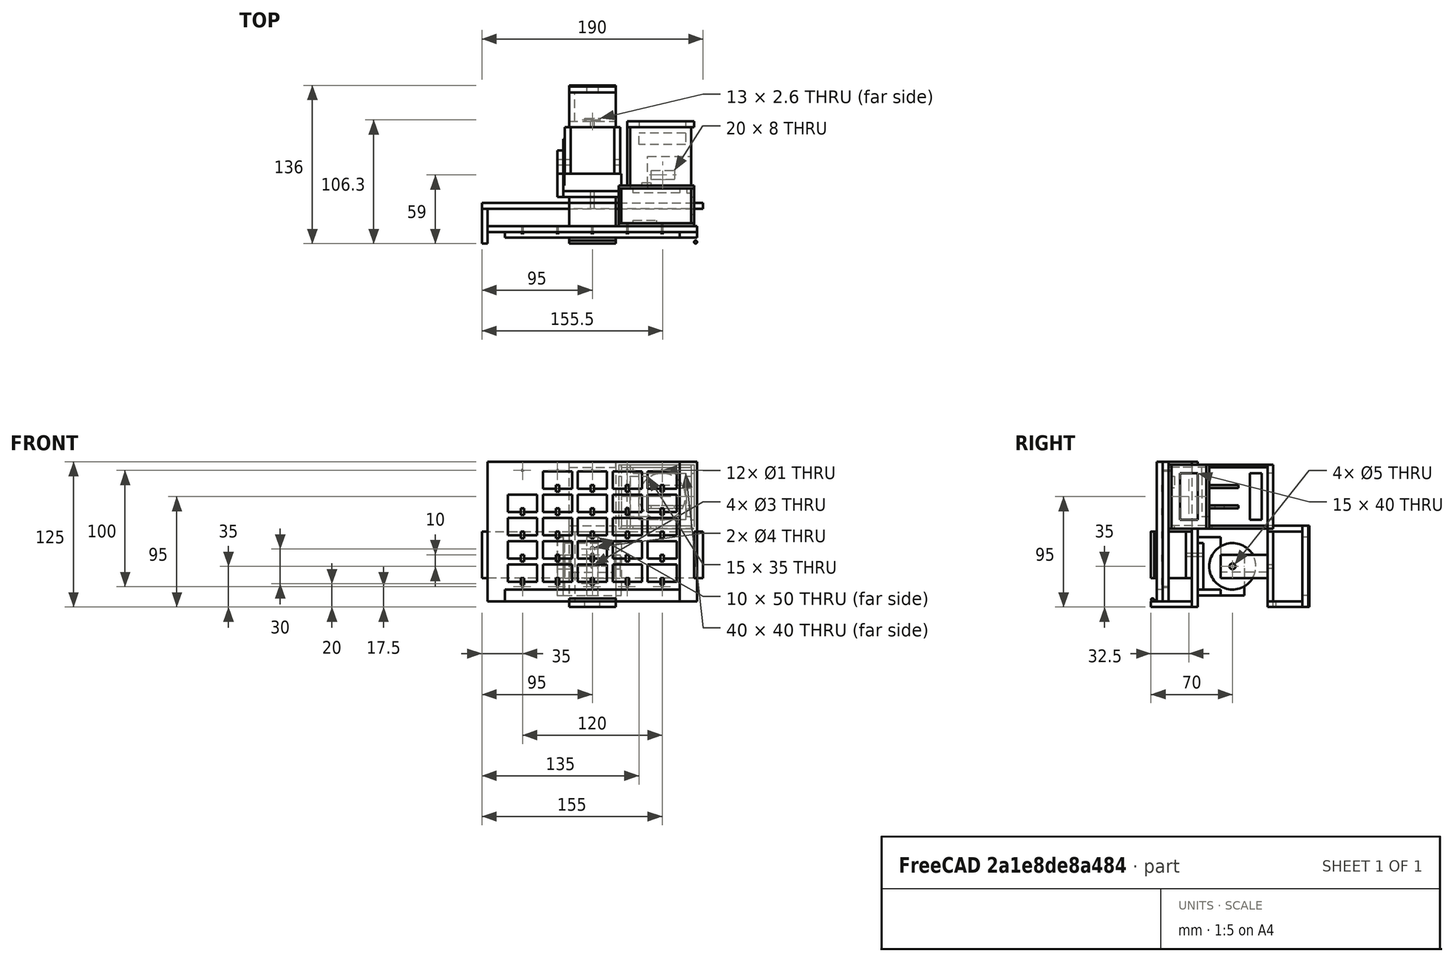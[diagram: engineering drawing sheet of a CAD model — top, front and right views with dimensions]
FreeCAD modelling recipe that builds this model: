
FCSTD DOCUMENT  (FreeCAD 0.15R4671 (Git))
Label: light
License: All rights reserved
LicenseURL: http://en.wikipedia.org/wiki/All_rights_reserved
objects: Sketcher::SketchObject×40, PartDesign::Pad×40, Part::FeaturePython×21, App::DocumentObjectGroup×10, Mesh::Feature×1
note: 141 computed .brp shape members not serialized (recipe doc carries the construction recipe); baked Part::Feature solids carry a one-line shape summary decoded from their .brp

FEATURE [Sketcher::SketchObject] Sketch
  Placement = pos=(0,0,0) rot=(1,0,0;1.5708rad)
  sketch-geometry (14):
    g0: LineSegment StartX=-90 StartY=60 StartZ=0 EndX=90 EndY=60 EndZ=0
    g1: LineSegment StartX=90 StartY=60 StartZ=0 EndX=90 EndY=-60 EndZ=0
    g2: LineSegment StartX=90 StartY=-60 StartZ=0 EndX=-90 EndY=-60 EndZ=0
    g3: LineSegment StartX=-90 StartY=-60 StartZ=0 EndX=-90 EndY=60 EndZ=0
    g4: Circle CenterX=-60 CenterY=52.5 CenterZ=0 NormalX=0 NormalY=0 NormalZ=1 Radius=0.5
    g5: Circle CenterX=-30 CenterY=52.5 CenterZ=0 NormalX=0 NormalY=0 NormalZ=1 Radius=0.5
    g6: Circle CenterX=0 CenterY=52.5 CenterZ=0 NormalX=0 NormalY=0 NormalZ=1 Radius=0.5
    g7: Circle CenterX=30 CenterY=52.5 CenterZ=0 NormalX=0 NormalY=0 NormalZ=1 Radius=0.5
    g8: Circle CenterX=60 CenterY=52.5 CenterZ=0 NormalX=0 NormalY=0 NormalZ=1 Radius=0.5
    g9: Circle CenterX=-60 CenterY=-47.5 CenterZ=0 NormalX=0 NormalY=0 NormalZ=1 Radius=0.5
    g10: Circle CenterX=-30 CenterY=-47.5 CenterZ=0 NormalX=0 NormalY=0 NormalZ=1 Radius=0.5
    g11: Circle CenterX=0 CenterY=-47.5 CenterZ=0 NormalX=0 NormalY=0 NormalZ=1 Radius=0.5
    g12: Circle CenterX=30 CenterY=-47.5 CenterZ=0 NormalX=0 NormalY=0 NormalZ=1 Radius=0.5
    g13: Circle CenterX=60 CenterY=-47.5 CenterZ=0 NormalX=0 NormalY=0 NormalZ=1 Radius=0.5
  constraints (36):
    c: Coincident(g0,g1)
    c: Coincident(g1,g2)
    c: Coincident(g2,g3)
    c: Coincident(g3,g0)
    c: Horizontal(g0)
    c: Horizontal(g2)
    c: Vertical(g1)
    c: Vertical(g3)
    c: Symmetric(g0,g0,g-2)
    c: DistanceX(g0,g0) = 180
    c: DistanceY(g3,g3) = 120
    c: Symmetric(g0,g2,g-1)
    c: Radius(g4) = 0.5
    c: Radius(g5) = 0.5
    c: DistanceY(g4,g0) = 7.5
    c: DistanceY(g5,g0) = 7.5
    c: DistanceX(g4,g5) = 30
    c: Equal(g5,g6) = 0.5
    c: DistanceY(g6,g0) = 7.5
    c: DistanceX(g5,g6) = 30
    c: DistanceY(g7,g0) = 7.5
    c: DistanceX(g6,g7) = 30
    c: DistanceY(g8,g0) = 7.5
    c: DistanceX(g7,g8) = 30
    c: Radius(g9) = 0.5
    c: DistanceY(g2,g9) = 12.5
    c: DistanceX(g2,g9) = 30
    c: Equal(g9,g10) = 0.5
    c: DistanceY(g2,g10) = 12.5
    c: DistanceX(g9,g10) = 30
    c: DistanceY(g2,g11) = 12.5
    c: DistanceX(g10,g11) = 30
    c: DistanceY(g1,g12) = 12.5
    c: DistanceX(g11,g12) = 30
    c: DistanceY(g1,g13) = 12.5
    c: DistanceX(g12,g13) = 30
FEATURE [PartDesign::Pad] Pad
  Length = 5
  Length2 = 100
  Placement = pos=(0,0,0) rot=(1,0,0;1.5708rad)
  Sketch = -> Sketch
  Type = 0
FEATURE [Sketcher::SketchObject] Sketch003
  Placement = pos=(0,-5,0) rot=(1,0,0;1.5708rad)
  sketch-geometry (4):
    g0: LineSegment StartX=-61.5 StartY=40 StartZ=0 EndX=-58.5 EndY=40 EndZ=0
    g1: LineSegment StartX=-58.5 StartY=40 StartZ=0 EndX=-58.5 EndY=34.3 EndZ=0
    g2: LineSegment StartX=-58.5 StartY=34.3 StartZ=0 EndX=-61.5 EndY=34.3 EndZ=0
    g3: LineSegment StartX=-61.5 StartY=34.3 StartZ=0 EndX=-61.5 EndY=40 EndZ=0
  constraints (12):
    c: Coincident(g0,g1)
    c: Coincident(g1,g2)
    c: Coincident(g2,g3)
    c: Coincident(g3,g0)
    c: Horizontal(g0)
    c: Horizontal(g2)
    c: Vertical(g1)
    c: Vertical(g3)
    c: DistanceX(g0,g0) = 3
    c: DistanceY(g3,g3) = 5.7
    c: DistanceY(g-1,g0) = 40
    c: DistanceX(g1,g-1) = 58.5
FEATURE [PartDesign::Pad] Pad003
  Length = 0.9
  Length2 = 100
  Placement = pos=(0,-5,0) rot=(1,0,0;1.5708rad)
  Sketch = -> Sketch003
  Type = 0
FEATURE [Part::FeaturePython] Clone  label="Clone of Pad003"  # Draft clone (typed FeaturePython)
  Objects = -> [Pad003]
  Placement = pos=(0,-5,-20) rot=(1,0,0;1.5708rad)
  Scale = (1,1,1)
FEATURE [Part::FeaturePython] Clone001  label="Clone of Pad004"  # Draft clone (typed FeaturePython)
  Objects = -> [Pad003]
  Placement = pos=(0,-5,-40) rot=(1,0,0;1.5708rad)
  Scale = (1,1,1)
FEATURE [Part::FeaturePython] Clone002  label="Clone of Pad005"  # Draft clone (typed FeaturePython)
  Objects = -> [Pad003]
  Placement = pos=(0,-5,-60) rot=(1,0,0;1.5708rad)
  Scale = (1,1,1)
FEATURE [Part::FeaturePython] Clone003  label="Clone of Pad006"  # Draft clone (typed FeaturePython)
  Objects = -> [Pad003]
  Placement = pos=(0,-5,-80) rot=(1,0,0;1.5708rad)
  Scale = (1,1,1)
FEATURE [Sketcher::SketchObject] Sketch004
  Placement = pos=(90,0,0) rot=(0.57735,0.57735,0.57735;2.0944rad)
  sketch-geometry (4):
    g0: LineSegment StartX=-15 StartY=0 StartZ=0 EndX=15 EndY=0 EndZ=0
    g1: LineSegment StartX=15 StartY=0 StartZ=0 EndX=15 EndY=-40 EndZ=0
    g2: LineSegment StartX=15 StartY=-40 StartZ=0 EndX=-15 EndY=-40 EndZ=0
    g3: LineSegment StartX=-15 StartY=-40 StartZ=0 EndX=-15 EndY=0 EndZ=0
  constraints (12):
    c: Coincident(g0,g1)
    c: Coincident(g1,g2)
    c: Coincident(g2,g3)
    c: Coincident(g3,g0)
    c: Horizontal(g0)
    c: Horizontal(g2)
    c: Vertical(g1)
    c: Vertical(g3)
    c: DistanceX(g0,g0) = 30
    c: DistanceY(g1,g1) = 40
    c: DistanceX(g-1,g0) = 15
    c: PointOnObject(g0,g-1)
FEATURE [PartDesign::Pad] Pad004
  Length = 5
  Length2 = 100
  Placement = pos=(90,0,0) rot=(0.57735,0.57735,0.57735;2.0944rad)
  Sketch = -> Sketch004
  Type = 0
FEATURE [Part::FeaturePython] Clone008  label="Clone of Pad007"  # Draft clone (typed FeaturePython)
  Objects = -> [Pad004]
  Placement = pos=(-95,0,0) rot=(0.57735,0.57735,0.57735;2.0944rad)
  Scale = (1,1,1)
FEATURE [Sketcher::SketchObject] Sketch005
  Placement = pos=(0,20,0) rot=(1,0,0;1.5708rad)
  sketch-geometry (5):
    g0: LineSegment StartX=-95 StartY=0 StartZ=0 EndX=95 EndY=0 EndZ=0
    g1: LineSegment StartX=95 StartY=0 StartZ=0 EndX=95 EndY=-40 EndZ=0
    g2: LineSegment StartX=95 StartY=-40 StartZ=0 EndX=-95 EndY=-40 EndZ=0
    g3: LineSegment StartX=-95 StartY=-40 StartZ=0 EndX=-95 EndY=0 EndZ=0
    g4: Circle CenterX=0 CenterY=-20 CenterZ=0 NormalX=0 NormalY=0 NormalZ=1 Radius=1.5
  constraints (15):
    c: Coincident(g0,g1)
    c: Coincident(g1,g2)
    c: Coincident(g2,g3)
    c: Coincident(g3,g0)
    c: Horizontal(g0)
    c: Horizontal(g2)
    c: Vertical(g1)
    c: Vertical(g3)
    c: DistanceX(g0,g0) = 190
    c: DistanceY(g3,g3) = 40
    c: Symmetric(g1,g2,g-2)
    c: PointOnObject(g0,g-1)
    c: PointOnObject(g4,g-2)
    c: Radius(g4) = 1.5
    c: DistanceY(g4,g0) = 20
FEATURE [PartDesign::Pad] Pad005
  Length = 5
  Length2 = 100
  Placement = pos=(0,20,0) rot=(1,0,0;1.5708rad)
  Sketch = -> Sketch005
  Type = 0
FEATURE [Sketcher::SketchObject] Sketch006
  Placement = pos=(0,0,55) rot=(0,0,1;0rad)
  sketch-geometry (4):
    g0: LineSegment StartX=-20 StartY=20 StartZ=0 EndX=20 EndY=20 EndZ=0
    g1: LineSegment StartX=20 StartY=20 StartZ=0 EndX=20 EndY=0 EndZ=0
    g2: LineSegment StartX=20 StartY=0 StartZ=0 EndX=-20 EndY=0 EndZ=0
    g3: LineSegment StartX=-20 StartY=0 StartZ=0 EndX=-20 EndY=20 EndZ=0
  constraints (12):
    c: Coincident(g0,g1)
    c: Coincident(g1,g2)
    c: Coincident(g2,g3)
    c: Coincident(g3,g0)
    c: Horizontal(g0)
    c: Horizontal(g2)
    c: Vertical(g1)
    c: Vertical(g3)
    c: PointOnObject(g1,g-1)
    c: Symmetric(g0,g0,g-2)
    c: DistanceX(g0,g0) = 40
    c: DistanceY(g3,g3) = 20
FEATURE [PartDesign::Pad] Pad006
  Length = 5
  Length2 = 100
  Placement = pos=(0,0,55) rot=(0,0,1;0rad)
  Sketch = -> Sketch006
  Type = 0
FEATURE [Sketcher::SketchObject] Sketch007
  Placement = pos=(0,25,0) rot=(1,0,0;1.5708rad)
  sketch-geometry (5):
    g0: LineSegment StartX=-20 StartY=60 StartZ=0 EndX=20 EndY=60 EndZ=0
    g1: LineSegment StartX=20 StartY=60 StartZ=0 EndX=20 EndY=-65 EndZ=0
    g2: LineSegment StartX=20 StartY=-65 StartZ=0 EndX=-20 EndY=-65 EndZ=0
    g3: LineSegment StartX=-20 StartY=-65 StartZ=0 EndX=-20 EndY=60 EndZ=0
    g4: Circle CenterX=0 CenterY=-20 CenterZ=0 NormalX=0 NormalY=0 NormalZ=1 Radius=1.5
  constraints (15):
    c: Coincident(g0,g1)
    c: Coincident(g1,g2)
    c: Coincident(g2,g3)
    c: Coincident(g3,g0)
    c: Horizontal(g0)
    c: Horizontal(g2)
    c: Vertical(g1)
    c: Vertical(g3)
    c: DistanceY(g3,g3) = 125
    c: Symmetric(g0,g0,g-2)
    c: DistanceX(g0,g0) = 40
    c: DistanceY(g1,g-1) = 65
    c: PointOnObject(g4,g-2)
    c: Radius(g4) = 1.5
    c: DistanceY(g4,g-1) = 20
FEATURE [PartDesign::Pad] Pad007
  Length = 5
  Length2 = 100
  Placement = pos=(0,25,0) rot=(1,0,0;1.5708rad)
  Sketch = -> Sketch007
  Type = 0
FEATURE [Sketcher::SketchObject] Sketch008
  Placement = pos=(25,0,0) rot=(0.57735,0.57735,0.57735;2.0944rad)
  sketch-geometry (7):
    g0: LineSegment StartX=65 StartY=-20 StartZ=0 EndX=65 EndY=-55 EndZ=0
    g1: LineSegment StartX=65 StartY=-55 StartZ=0 EndX=25 EndY=-55 EndZ=0
    g2: LineSegment StartX=25 StartY=-55 StartZ=0 EndX=25 EndY=-5 EndZ=0
    g3: Circle CenterX=55 CenterY=-30 CenterZ=0 NormalX=0 NormalY=0 NormalZ=1 Radius=2.5
    g4: LineSegment StartX=25 StartY=-5 StartZ=0 EndX=45 EndY=-5 EndZ=0
    g5: LineSegment StartX=45 StartY=-5 StartZ=0 EndX=45 EndY=-20 EndZ=0
    g6: LineSegment StartX=45 StartY=-20 StartZ=0 EndX=65 EndY=-20 EndZ=0
  constraints (21):
    c: Coincident(g0,g1)
    c: Coincident(g1,g2)
    c: Horizontal(g1)
    c: Vertical(g0)
    c: Vertical(g2)
    c: DistanceX(g2,g0) = 40
    c: DistanceY(g0,g0) = 35
    c: DistanceX(g1) = 25
    c: Radius(g3) = 2.5
    c: DistanceX(g3,g0) = 10
    c: DistanceY(g3,g0) = 10
    c: DistanceY(g0,g-1) = 20
    c: Horizontal(g4)
    c: Coincident(g4,g5)
    c: Vertical(g5)
    c: Coincident(g5,g6)
    c: Horizontal(g6)
    c: DistanceY(g5) = -15
    c: Coincident(g2,g4)
    c: Coincident(g0,g6)
    c: DistanceX(g4) = 20
FEATURE [PartDesign::Pad] Pad008
  Length = 5
  Length2 = 100
  Placement = pos=(25,0,0) rot=(0.57735,0.57735,0.57735;2.0944rad)
  Sketch = -> Sketch008
  Type = 0
FEATURE [Sketcher::SketchObject] Sketch010
  Placement = pos=(0,0,-10) rot=(0,0,1;0rad)
  sketch-geometry (4):
    g0: LineSegment StartX=-25 StartY=45 StartZ=0 EndX=25 EndY=45 EndZ=0
    g1: LineSegment StartX=25 StartY=45 StartZ=0 EndX=25 EndY=25 EndZ=0
    g2: LineSegment StartX=25 StartY=25 StartZ=0 EndX=-25 EndY=25 EndZ=0
    g3: LineSegment StartX=-25 StartY=25 StartZ=0 EndX=-25 EndY=45 EndZ=0
  constraints (12):
    c: Coincident(g0,g1)
    c: Coincident(g1,g2)
    c: Coincident(g2,g3)
    c: Coincident(g3,g0)
    c: Horizontal(g0)
    c: Horizontal(g2)
    c: Vertical(g1)
    c: Vertical(g3)
    c: DistanceX(g0,g0) = 50
    c: DistanceY(g3,g3) = 20
    c: Symmetric(g1,g2,g-2)
    c: DistanceY(g-1,g2) = 25
FEATURE [PartDesign::Pad] Pad010
  Length = 5
  Length2 = 100
  Placement = pos=(0,0,-10) rot=(0,0,1;0rad)
  Sketch = -> Sketch010
  Type = 0
FEATURE [Part::FeaturePython] Clone010  label="Clone of Pad010"  # Draft clone (typed FeaturePython)
  Objects = -> [Pad010]
  Placement = pos=(0,0,-55) rot=(0,0,1;0rad)
  Scale = (1,1,1)
FEATURE [Sketcher::SketchObject] Sketch011
  Placement = pos=(18.75,0,0) rot=(0.57735,0.57735,0.57735;2.0944rad)
  sketch-geometry (5):
    g0: LineSegment StartX=45 StartY=-20 StartZ=0 EndX=85 EndY=-20 EndZ=0
    g1: LineSegment StartX=85 StartY=-20 StartZ=0 EndX=85 EndY=-40 EndZ=0
    g2: LineSegment StartX=85 StartY=-40 StartZ=0 EndX=45 EndY=-40 EndZ=0
    g3: LineSegment StartX=45 StartY=-40 StartZ=0 EndX=45 EndY=-20 EndZ=0
    g4: Circle CenterX=55 CenterY=-30 CenterZ=0 NormalX=0 NormalY=0 NormalZ=1 Radius=2.5
  constraints (15):
    c: Coincident(g0,g1)
    c: Coincident(g1,g2)
    c: Coincident(g2,g3)
    c: Coincident(g3,g0)
    c: Horizontal(g0)
    c: Horizontal(g2)
    c: Vertical(g1)
    c: Vertical(g3)
    c: DistanceY(g1,g1) = 20
    c: DistanceX(g0,g0) = 40
    c: DistanceX(g-1,g0) = 45
    c: Radius(g4) = 2.5
    c: DistanceX(g0,g4) = 10
    c: DistanceY(g0,g-1) = 20
    c: DistanceY(g4,g0) = 10
FEATURE [PartDesign::Pad] Pad011
  Length = 5
  Length2 = 100
  Placement = pos=(18.75,0,0) rot=(0.57735,0.57735,0.57735;2.0944rad)
  Sketch = -> Sketch011
  Type = 0
FEATURE [Sketcher::SketchObject] Sketch012
  Placement = pos=(0,0,-25) rot=(0,0,1;0rad)
  sketch-geometry (4):
    g0: LineSegment StartX=-18.75 StartY=85 StartZ=0 EndX=18.75 EndY=85 EndZ=0
    g1: LineSegment StartX=18.75 StartY=85 StartZ=0 EndX=18.75 EndY=45 EndZ=0
    g2: LineSegment StartX=18.75 StartY=45 StartZ=0 EndX=-18.75 EndY=45 EndZ=0
    g3: LineSegment StartX=-18.75 StartY=45 StartZ=0 EndX=-18.75 EndY=85 EndZ=0
  constraints (12):
    c: Coincident(g0,g1)
    c: Coincident(g1,g2)
    c: Coincident(g2,g3)
    c: Coincident(g3,g0)
    c: Horizontal(g0)
    c: Horizontal(g2)
    c: Vertical(g1)
    c: Vertical(g3)
    c: DistanceX(g0,g0) = 37.5
    c: DistanceY(g3,g3) = 40
    c: Symmetric(g0,g0,g-2)
    c: DistanceY(g-1,g1) = 45
FEATURE [PartDesign::Pad] Pad012
  Length = 5
  Length2 = 100
  Placement = pos=(0,0,-25) rot=(0,0,1;0rad)
  Sketch = -> Sketch012
  Type = 0
FEATURE [Part::FeaturePython] Clone012  label="Clone of Pad012"  # Draft clone (typed FeaturePython)
  Objects = -> [Pad012]
  Placement = pos=(0,0,-40) rot=(0,0,1;0rad)
  Scale = (1,1,1)
FEATURE [Part::FeaturePython] Clone013  label="Clone of Pad013"  # Draft clone (typed FeaturePython)
  Objects = -> [Pad008]
  Placement = pos=(-30,0,0) rot=(0.57735,0.57735,0.57735;2.0944rad)
  Scale = (1,1,1)
FEATURE [Sketcher::SketchObject] Sketch013
  Placement = pos=(0,0,-65) rot=(0,0,1;0rad)
  sketch-geometry (4):
    g0: LineSegment StartX=-20 StartY=20 StartZ=0 EndX=20 EndY=20 EndZ=0
    g1: LineSegment StartX=20 StartY=20 StartZ=0 EndX=20 EndY=-15 EndZ=0
    g2: LineSegment StartX=20 StartY=-15 StartZ=0 EndX=-20 EndY=-15 EndZ=0
    g3: LineSegment StartX=-20 StartY=-15 StartZ=0 EndX=-20 EndY=20 EndZ=0
  constraints (12):
    c: Coincident(g0,g1)
    c: Coincident(g1,g2)
    c: Coincident(g2,g3)
    c: Coincident(g3,g0)
    c: Horizontal(g0)
    c: Horizontal(g2)
    c: Vertical(g1)
    c: Vertical(g3)
    c: Symmetric(g0,g0,g-2)
    c: DistanceX(g0,g0) = 40
    c: DistanceY(g3,g3) = 35
    c: DistanceY(g-1,g0) = 20
FEATURE [PartDesign::Pad] Pad013
  Length = 5
  Length2 = 100
  Placement = pos=(0,0,-65) rot=(0,0,1;0rad)
  Sketch = -> Sketch013
  Type = 0
FEATURE [Sketcher::SketchObject] Sketch014
  Placement = pos=(0,0,-40) rot=(0,0,1;0rad)
  sketch-geometry (1):
    g0: Circle CenterX=-88.7 CenterY=-13.7 CenterZ=0 NormalX=0 NormalY=0 NormalZ=1 Radius=1.3
  constraints (3):
    c: Radius(g0) = 1.3
    c: DistanceX(g0) = -88.7
    c: DistanceY(g0) = -13.7
FEATURE [PartDesign::Pad] Pad014
  Length = 40
  Length2 = 100
  Placement = pos=(0,0,-40) rot=(0,0,1;0rad)
  Sketch = -> Sketch014
  Type = 0
FEATURE [Part::FeaturePython] Clone014  label="Clone of Pad014"  # Draft clone (typed FeaturePython)
  Objects = -> [Pad014]
  Placement = pos=(177.4,0,-40) rot=(0,0,1;0rad)
  Scale = (1,1,1)
FEATURE [App::DocumentObjectGroup] Group002  label="HFrame"
  Group = -> [Pad005,Pad004,Clone008,Pad014,Clone014]
FEATURE [Sketcher::SketchObject] Sketch015
  Placement = pos=(-20,0,0) rot=(0.57735,0.57735,0.57735;2.0944rad)
  sketch-geometry (1):
    g0: Circle CenterX=-13.7 CenterY=-58.7 CenterZ=0 NormalX=0 NormalY=0 NormalZ=1 Radius=1.3
  constraints (3):
    c: Radius(g0) = 1.3
    c: DistanceX(g0) = -13.7
    c: DistanceY(g0) = -58.7
FEATURE [PartDesign::Pad] Pad015
  Length = 40
  Length2 = 100
  Placement = pos=(-20,0,0) rot=(0.57735,0.57735,0.57735;2.0944rad)
  Sketch = -> Sketch015
  Type = 0
FEATURE [App::DocumentObjectGroup] Group003  label="VFrame"
  Group = -> [Pad006,Pad007,Pad013,Pad015]
FEATURE [Sketcher::SketchObject] Sketch016
  Placement = pos=(0,90,0) rot=(1,0,0;1.5708rad)
  sketch-geometry (5):
    g0: LineSegment StartX=-20 StartY=0 StartZ=0 EndX=20 EndY=0 EndZ=0
    g1: LineSegment StartX=20 StartY=0 StartZ=0 EndX=20 EndY=-60 EndZ=0
    g2: LineSegment StartX=20 StartY=-60 StartZ=0 EndX=-20 EndY=-60 EndZ=0
    g3: LineSegment StartX=-20 StartY=-60 StartZ=0 EndX=-20 EndY=0 EndZ=0
    g4: Circle CenterX=0 CenterY=-30 CenterZ=0 NormalX=0 NormalY=0 NormalZ=1 Radius=1.5
  constraints (14):
    c: Coincident(g0,g1)
    c: Coincident(g1,g2)
    c: Coincident(g2,g3)
    c: Coincident(g3,g0)
    c: Horizontal(g0)
    c: Horizontal(g2)
    c: Vertical(g1)
    c: Vertical(g3)
    c: Symmetric(g0,g0,g-2)
    c: DistanceX(g0,g0) = 40
    c: DistanceY(g1,g1) = 60
    c: DistanceY(g0) = 0
    c: Radius(g4) = 1.5
    c: DistanceY(g4,g0) = 30
FEATURE [PartDesign::Pad] Pad016
  Length = 5
  Length2 = 100
  Placement = pos=(0,90,0) rot=(1,0,0;1.5708rad)
  Sketch = -> Sketch016
  Type = 0
FEATURE [Sketcher::SketchObject] Sketch017
  Placement = pos=(15,0,0) rot=(0.57735,0.57735,0.57735;2.0944rad)
  sketch-geometry (4):
    g0: LineSegment StartX=90 StartY=0 StartZ=0 EndX=115 EndY=0 EndZ=0
    g1: LineSegment StartX=115 StartY=0 StartZ=0 EndX=115 EndY=-60 EndZ=0
    g2: LineSegment StartX=115 StartY=-60 StartZ=0 EndX=90 EndY=-60 EndZ=0
    g3: LineSegment StartX=90 StartY=-60 StartZ=0 EndX=90 EndY=0 EndZ=0
  constraints (12):
    c: Coincident(g0,g1)
    c: Coincident(g1,g2)
    c: Coincident(g2,g3)
    c: Coincident(g3,g0)
    c: Horizontal(g0)
    c: Horizontal(g2)
    c: Vertical(g1)
    c: Vertical(g3)
    c: PointOnObject(g0,g-1)
    c: DistanceX(g0,g0) = 25
    c: DistanceY(g1,g1) = 60
    c: DistanceX(g-1,g0) = 90
FEATURE [PartDesign::Pad] Pad017
  Length = 5
  Length2 = 100
  Placement = pos=(15,0,0) rot=(0.57735,0.57735,0.57735;2.0944rad)
  Sketch = -> Sketch017
  Type = 0
FEATURE [Part::FeaturePython] Clone015  label="Clone of Pad017"  # Draft clone (typed FeaturePython)
  Objects = -> [Pad017]
  Placement = pos=(-20,0,0) rot=(0.57735,0.57735,0.57735;2.0944rad)
  Scale = (1,1,1)
FEATURE [Sketcher::SketchObject] Sketch018
  sketch-geometry (4):
    g0: LineSegment StartX=-20 StartY=115 StartZ=0 EndX=20 EndY=115 EndZ=0
    g1: LineSegment StartX=20 StartY=115 StartZ=0 EndX=20 EndY=85 EndZ=0
    g2: LineSegment StartX=20 StartY=85 StartZ=0 EndX=-20 EndY=85 EndZ=0
    g3: LineSegment StartX=-20 StartY=85 StartZ=0 EndX=-20 EndY=115 EndZ=0
  constraints (12):
    c: Coincident(g0,g1)
    c: Coincident(g1,g2)
    c: Coincident(g2,g3)
    c: Coincident(g3,g0)
    c: Horizontal(g0)
    c: Horizontal(g2)
    c: Vertical(g1)
    c: Vertical(g3)
    c: DistanceX(g0,g0) = 40
    c: DistanceY(g3,g3) = 30
    c: DistanceY(g-1,g1) = 85
    c: Symmetric(g1,g2,g-2)
FEATURE [PartDesign::Pad] Pad018
  Length = 5
  Length2 = 100
  Sketch = -> Sketch018
  Type = 0
FEATURE [Sketcher::SketchObject] Sketch019
  Placement = pos=(0,120,0) rot=(1,0,0;1.5708rad)
  sketch-geometry (8):
    g0: LineSegment StartX=-20 StartY=5 StartZ=0 EndX=20 EndY=5 EndZ=0
    g1: LineSegment StartX=20 StartY=5 StartZ=0 EndX=20 EndY=-65 EndZ=0
    g2: LineSegment StartX=20 StartY=-65 StartZ=0 EndX=-20 EndY=-65 EndZ=0
    g3: LineSegment StartX=-20 StartY=-65 StartZ=0 EndX=-20 EndY=5 EndZ=0
    g4: LineSegment StartX=5 StartY=-5 StartZ=0 EndX=-5 EndY=-5 EndZ=0
    g5: LineSegment StartX=-5 StartY=-5 StartZ=0 EndX=-5 EndY=-55 EndZ=0
    g6: LineSegment StartX=-5 StartY=-55 StartZ=0 EndX=5 EndY=-55 EndZ=0
    g7: LineSegment StartX=5 StartY=-55 StartZ=0 EndX=5 EndY=-5 EndZ=0
  constraints (24):
    c: Coincident(g0,g1)
    c: Coincident(g1,g2)
    c: Coincident(g2,g3)
    c: Coincident(g3,g0)
    c: Horizontal(g0)
    c: Horizontal(g2)
    c: Vertical(g1)
    c: Vertical(g3)
    c: Symmetric(g0,g0,g-2)
    c: DistanceX(g0,g0) = 40
    c: DistanceY(g1,g1) = 70
    c: DistanceY(g0) = 5
    c: Coincident(g4,g5)
    c: Coincident(g5,g6)
    c: Coincident(g6,g7)
    c: Coincident(g7,g4)
    c: Horizontal(g4)
    c: Horizontal(g6)
    c: Vertical(g5)
    c: Vertical(g7)
    c: Symmetric(g4,g4,g-2)
    c: DistanceX(g4,g4) = 10
    c: DistanceY(g5,g5) = 50
    c: DistanceY(g4,g0) = 10
FEATURE [PartDesign::Pad] Pad019
  Length = 5
  Length2 = 100
  Placement = pos=(0,120,0) rot=(1,0,0;1.5708rad)
  Sketch = -> Sketch019
  Type = 0
FEATURE [Sketcher::SketchObject] Sketch020
  Placement = pos=(0,121,0) rot=(1,0,0;1.5708rad)
  sketch-geometry (6):
    g0: LineSegment StartX=-20 StartY=5 StartZ=0 EndX=20 EndY=5 EndZ=0
    g1: LineSegment StartX=20 StartY=5 StartZ=0 EndX=20 EndY=-65 EndZ=0
    g2: LineSegment StartX=20 StartY=-65 StartZ=0 EndX=-20 EndY=-65 EndZ=0
    g3: LineSegment StartX=-20 StartY=-65 StartZ=0 EndX=-20 EndY=5 EndZ=0
    g4: Circle CenterX=0 CenterY=-15 CenterZ=0 NormalX=0 NormalY=0 NormalZ=1 Radius=2
    g5: Circle CenterX=0 CenterY=-45 CenterZ=0 NormalX=0 NormalY=0 NormalZ=1 Radius=2
  constraints (17):
    c: Coincident(g0,g1)
    c: Coincident(g1,g2)
    c: Coincident(g2,g3)
    c: Coincident(g3,g0)
    c: Horizontal(g0)
    c: Horizontal(g2)
    c: Vertical(g1)
    c: Vertical(g3)
    c: Symmetric(g0,g0,g-2)
    c: DistanceX(g0,g0) = 40
    c: DistanceY(g1,g1) = 70
    c: DistanceY(g0) = 5
    c: Radius(g4) = 2
    c: DistanceY(g4,g0) = 20
    c: PointOnObject(g5,g-2)
    c: Radius(g5) = 2
    c: DistanceY(g2,g5) = 20
FEATURE [PartDesign::Pad] Pad020
  Length = 1
  Length2 = 100
  Placement = pos=(0,121,0) rot=(1,0,0;1.5708rad)
  Sketch = -> Sketch020
  Type = 0
FEATURE [Sketcher::SketchObject] Sketch021
  Placement = pos=(-23.75,0,0) rot=(0.57735,0.57735,0.57735;2.0944rad)
  sketch-geometry (5):
    g0: LineSegment StartX=45 StartY=-20 StartZ=0 EndX=85 EndY=-20 EndZ=0
    g1: LineSegment StartX=85 StartY=-20 StartZ=0 EndX=85 EndY=-40 EndZ=0
    g2: LineSegment StartX=85 StartY=-40 StartZ=0 EndX=45 EndY=-40 EndZ=0
    g3: LineSegment StartX=45 StartY=-40 StartZ=0 EndX=45 EndY=-20 EndZ=0
    g4: Circle CenterX=55 CenterY=-30 CenterZ=0 NormalX=0 NormalY=0 NormalZ=1 Radius=2.5
  constraints (15):
    c: Coincident(g0,g1)
    c: Coincident(g1,g2)
    c: Coincident(g2,g3)
    c: Coincident(g3,g0)
    c: Horizontal(g0)
    c: Horizontal(g2)
    c: Vertical(g1)
    c: Vertical(g3)
    c: DistanceY(g1,g1) = 20
    c: DistanceX(g0,g0) = 40
    c: DistanceX(g-1,g0) = 45
    c: Radius(g4) = 2.5
    c: DistanceX(g0,g4) = 10
    c: DistanceY(g0,g-1) = 20
    c: DistanceY(g4,g0) = 10
FEATURE [PartDesign::Pad] Pad021
  Length = 5
  Length2 = 100
  Placement = pos=(-23.75,0,0) rot=(0.57735,0.57735,0.57735;2.0944rad)
  Sketch = -> Sketch021
  Type = 0
FEATURE [App::DocumentObjectGroup] Group006  label="Plug"
  Group = -> [Pad011,Pad012,Clone012,Pad021]
FEATURE [Sketcher::SketchObject] Sketch023
  Placement = pos=(0,-5,0) rot=(1,0,0;1.5708rad)
  sketch-geometry (4):
    g0: LineSegment StartX=-72.5 StartY=51.6323 StartZ=0 EndX=-47.5 EndY=51.6323 EndZ=0
    g1: LineSegment StartX=-47.5 StartY=51.6323 StartZ=0 EndX=-47.5 EndY=36.6323 EndZ=0
    g2: LineSegment StartX=-47.5 StartY=36.6323 StartZ=0 EndX=-72.5 EndY=36.6323 EndZ=0
    g3: LineSegment StartX=-72.5 StartY=36.6323 StartZ=0 EndX=-72.5 EndY=51.6323 EndZ=0
  constraints (11):
    c: Coincident(g0,g1)
    c: Coincident(g1,g2)
    c: Coincident(g2,g3)
    c: Coincident(g3,g0)
    c: Horizontal(g0)
    c: Horizontal(g2)
    c: Vertical(g1)
    c: Vertical(g3)
    c: DistanceX(g2,g2) = 25
    c: DistanceY(g1,g1) = 15
    c: DistanceX(g1,g-1) = 47.5
FEATURE [PartDesign::Pad] Pad023
  Length = 0.1
  Length2 = 100
  Placement = pos=(0,-5,0) rot=(1,0,0;1.5708rad)
  Sketch = -> Sketch023
  Type = 0
FEATURE [Part::FeaturePython] Clone017  label="Clone of Pad023"  # Draft clone (typed FeaturePython)
  Objects = -> [Pad023]
  Placement = pos=(0,-5,-20) rot=(1,0,0;1.5708rad)
  Scale = (1,1,1)
FEATURE [Part::FeaturePython] Clone018  label="Clone of Pad024"  # Draft clone (typed FeaturePython)
  Objects = -> [Pad023]
  Placement = pos=(0,-5,-40) rot=(1,0,0;1.5708rad)
  Scale = (1,1,1)
FEATURE [Part::FeaturePython] Clone019  label="Clone of Pad025"  # Draft clone (typed FeaturePython)
  Objects = -> [Pad023]
  Placement = pos=(0,-5,-60) rot=(1,0,0;1.5708rad)
  Scale = (1,1,1)
FEATURE [Part::FeaturePython] Clone020  label="Clone of Pad026"  # Draft clone (typed FeaturePython)
  Objects = -> [Pad023]
  Placement = pos=(0,-5,-80) rot=(1,0,0;1.5708rad)
  Scale = (1,1,1)
FEATURE [App::DocumentObjectGroup] Group  label="Array"
  Group = -> [Pad003,Clone,Clone001,Clone002,Clone003,Pad023,Clone017,Clone018,Clone019,Clone020]
FEATURE [Part::FeaturePython] Clone021  label="Clone of Array"  # Draft clone (typed FeaturePython)
  Objects = -> [Group]
  Placement = pos=(30,0,0) rot=(0,0,1;0rad)
  Scale = (1,1,1)
FEATURE [Part::FeaturePython] Clone022  label="Clone of Array001"  # Draft clone (typed FeaturePython)
  Objects = -> [Group]
  Placement = pos=(60,0,0) rot=(0,0,1;0rad)
  Scale = (1,1,1)
FEATURE [Part::FeaturePython] Clone023  label="Clone of Array002"  # Draft clone (typed FeaturePython)
  Objects = -> [Group]
  Placement = pos=(90,0,0) rot=(0,0,1;0rad)
  Scale = (1,1,1)
FEATURE [Part::FeaturePython] Clone024  label="Clone of Array003"  # Draft clone (typed FeaturePython)
  Objects = -> [Group]
  Placement = pos=(120,0,0) rot=(0,0,1;0rad)
  Scale = (1,1,1)
FEATURE [App::DocumentObjectGroup] Group001  label="LedArray"
  Group = -> [Group,Clone021,Clone022,Clone023,Clone024]
FEATURE [Sketcher::SketchObject] Sketch024
  Placement = pos=(0,-5,0) rot=(1,0,0;1.5708rad)
  sketch-geometry (4):
    g0: LineSegment StartX=-90 StartY=60 StartZ=0 EndX=-75 EndY=60 EndZ=0
    g1: LineSegment StartX=-75 StartY=60 StartZ=0 EndX=-75 EndY=-60 EndZ=0
    g2: LineSegment StartX=-75 StartY=-60 StartZ=0 EndX=-90 EndY=-60 EndZ=0
    g3: LineSegment StartX=-90 StartY=-60 StartZ=0 EndX=-90 EndY=60 EndZ=0
  constraints (12):
    c: Coincident(g0,g1)
    c: Coincident(g1,g2)
    c: Coincident(g2,g3)
    c: Coincident(g3,g0)
    c: Horizontal(g0)
    c: Horizontal(g2)
    c: Vertical(g1)
    c: Vertical(g3)
    c: DistanceX(g2,g2) = 15
    c: DistanceY(g1,g1) = 120
    c: Symmetric(g0,g2,g-1)
    c: DistanceX(g0,g-1) = 75
FEATURE [PartDesign::Pad] Pad024
  Length = 5
  Length2 = 100
  Placement = pos=(0,-5,0) rot=(1,0,0;1.5708rad)
  Sketch = -> Sketch024
  Type = 0
FEATURE [Part::FeaturePython] Clone025  label="Clone of Pad027"  # Draft clone (typed FeaturePython)
  Objects = -> [Pad024]
  Placement = pos=(165,-5,0) rot=(1,0,0;1.5708rad)
  Scale = (1,1,1)
FEATURE [Sketcher::SketchObject] Sketch025
  Placement = pos=(0,-5,0) rot=(1,0,0;1.5708rad)
  sketch-geometry (4):
    g0: LineSegment StartX=-75 StartY=-50 StartZ=0 EndX=75 EndY=-50 EndZ=0
    g1: LineSegment StartX=75 StartY=-50 StartZ=0 EndX=75 EndY=-60 EndZ=0
    g2: LineSegment StartX=75 StartY=-60 StartZ=0 EndX=-75 EndY=-60 EndZ=0
    g3: LineSegment StartX=-75 StartY=-60 StartZ=0 EndX=-75 EndY=-50 EndZ=0
  constraints (12):
    c: Coincident(g0,g1)
    c: Coincident(g1,g2)
    c: Coincident(g2,g3)
    c: Coincident(g3,g0)
    c: Horizontal(g0)
    c: Horizontal(g2)
    c: Vertical(g1)
    c: Vertical(g3)
    c: DistanceY(g1,g1) = 10
    c: DistanceX(g0,g0) = 150
    c: Symmetric(g2,g1,g-2)
    c: DistanceY(g2,g-1) = 60
FEATURE [PartDesign::Pad] Pad025
  Length = 5
  Length2 = 100
  Placement = pos=(0,-5,0) rot=(1,0,0;1.5708rad)
  Sketch = -> Sketch025
  Type = 0
FEATURE [App::DocumentObjectGroup] Group004  label="Frame"
  Group = -> [Pad,Pad024,Clone025,Pad025]
FEATURE [Sketcher::SketchObject] Sketch026
  Placement = pos=(0,0,-65) rot=(0,0,1;0rad)
  sketch-geometry (8):
    g0: LineSegment StartX=-20 StartY=115 StartZ=0 EndX=20 EndY=115 EndZ=0
    g1: LineSegment StartX=20 StartY=115 StartZ=0 EndX=20 EndY=85 EndZ=0
    g2: LineSegment StartX=20 StartY=85 StartZ=0 EndX=-20 EndY=85 EndZ=0
    g3: LineSegment StartX=-20 StartY=85 StartZ=0 EndX=-20 EndY=115 EndZ=0
    g4: LineSegment StartX=-6.5 StartY=92.6 StartZ=0 EndX=6.5 EndY=92.6 EndZ=0
    g5: LineSegment StartX=6.5 StartY=92.6 StartZ=0 EndX=6.5 EndY=90 EndZ=0
    g6: LineSegment StartX=6.5 StartY=90 StartZ=0 EndX=-6.5 EndY=90 EndZ=0
    g7: LineSegment StartX=-6.5 StartY=90 StartZ=0 EndX=-6.5 EndY=92.6 EndZ=0
  constraints (24):
    c: Coincident(g0,g1)
    c: Coincident(g1,g2)
    c: Coincident(g2,g3)
    c: Coincident(g3,g0)
    c: Horizontal(g0)
    c: Horizontal(g2)
    c: Vertical(g1)
    c: Vertical(g3)
    c: DistanceX(g0,g0) = 40
    c: DistanceY(g3,g3) = 30
    c: DistanceY(g-1,g1) = 85
    c: Symmetric(g1,g2,g-2)
    c: Coincident(g4,g5)
    c: Coincident(g5,g6)
    c: Coincident(g6,g7)
    c: Coincident(g7,g4)
    c: Horizontal(g4)
    c: Horizontal(g6)
    c: Vertical(g5)
    c: Vertical(g7)
    c: DistanceX(g4,g4) = 13
    c: DistanceY(g7,g7) = 2.6
    c: DistanceY(g2,g6) = 5
    c: DistanceX(g2,g6) = 13.5
FEATURE [PartDesign::Pad] Pad026
  Length = 5
  Length2 = 100
  Placement = pos=(0,0,-65) rot=(0,0,1;0rad)
  Sketch = -> Sketch026
  Type = 0
FEATURE [App::DocumentObjectGroup] Group007  label="Connector"
  Group = -> [Pad016,Pad017,Clone015,Pad018,Pad019,Pad020,Pad026]
FEATURE [Sketcher::SketchObject] Sketch027
  Placement = pos=(0,2.5,0) rot=(1,0,0;1.5708rad)
  sketch-geometry (6):
    g0: LineSegment StartX=22.5 StartY=57.5 StartZ=0 EndX=87.5 EndY=57.5 EndZ=0
    g1: LineSegment StartX=87.5 StartY=57.5 StartZ=0 EndX=87.5 EndY=2.5 EndZ=0
    g2: LineSegment StartX=87.5 StartY=2.5 StartZ=0 EndX=22.5 EndY=2.5 EndZ=0
    g3: LineSegment StartX=22.5 StartY=2.5 StartZ=0 EndX=22.5 EndY=57.5 EndZ=0
    g4: Circle CenterX=30 CenterY=52.5 CenterZ=0 NormalX=0 NormalY=0 NormalZ=1 Radius=0.5
    g5: Circle CenterX=60 CenterY=52.5 CenterZ=0 NormalX=0 NormalY=0 NormalZ=1 Radius=0.5
  constraints (18):
    c: Coincident(g0,g1)
    c: Coincident(g1,g2)
    c: Coincident(g2,g3)
    c: Coincident(g3,g0)
    c: Horizontal(g0)
    c: Horizontal(g2)
    c: Vertical(g1)
    c: Vertical(g3)
    c: DistanceX(g-1,g0) = 22.5
    c: DistanceX(g0,g0) = 65
    c: DistanceY(g1,g1) = 55
    c: DistanceY(g-1,g1) = 2.5
    c: DistanceX(g0,g4) = 7.5
    c: DistanceY(g4,g0) = 5
    c: Radius(g4) = 0.5
    c: Radius(g5) = 0.5
    c: DistanceX(g5,g0) = 27.5
    c: DistanceY(g5,g0) = 5
FEATURE [PartDesign::Pad] Pad027
  Length = 2.5
  Length2 = 100
  Placement = pos=(0,2.5,0) rot=(1,0,0;1.5708rad)
  Sketch = -> Sketch027
  Type = 0
FEATURE [Sketcher::SketchObject] Sketch028
  Placement = pos=(0,0,2.5) rot=(0,0,1;0rad)
  sketch-geometry (8):
    g0: LineSegment StartX=25 StartY=32.5 StartZ=0 EndX=85 EndY=32.5 EndZ=0
    g1: LineSegment StartX=85 StartY=32.5 StartZ=0 EndX=85 EndY=2.5 EndZ=0
    g2: LineSegment StartX=25 StartY=2.5 StartZ=0 EndX=25 EndY=32.5 EndZ=0
    g3: LineSegment StartX=25 StartY=2.5 StartZ=0 EndX=35 EndY=2.5 EndZ=0
    g4: LineSegment StartX=35 StartY=2.5 StartZ=0 EndX=35 EndY=5 EndZ=0
    g5: LineSegment StartX=35 StartY=5 StartZ=0 EndX=55 EndY=5 EndZ=0
    g6: LineSegment StartX=55 StartY=5 StartZ=0 EndX=55 EndY=2.5 EndZ=0
    g7: LineSegment StartX=55 StartY=2.5 StartZ=0 EndX=85 EndY=2.5 EndZ=0
  constraints (24):
    c: Coincident(g0,g1)
    c: Coincident(g2,g0)
    c: Horizontal(g0)
    c: Vertical(g1)
    c: Vertical(g2)
    c: DistanceY(g-1,g1) = 2.5
    c: DistanceX(g0,g0) = 60
    c: DistanceY(g2,g2) = 30
    c: DistanceX(g-1,g0) = 25
    c: Horizontal(g3)
    c: Coincident(g3,g4)
    c: Vertical(g4)
    c: Coincident(g4,g5)
    c: Horizontal(g5)
    c: Coincident(g5,g6)
    c: Vertical(g6)
    c: Coincident(g6,g7)
    c: Horizontal(g7)
    c: Coincident(g1,g7)
    c: Coincident(g2,g3)
    c: DistanceX(g3,g3) = 10
    c: DistanceX(g5,g5) = 20
    c: DistanceY(g6,g6) = 2.5
    c: Equal(g4,g6)
FEATURE [PartDesign::Pad] Pad028
  Length = 2.5
  Length2 = 100
  Placement = pos=(0,0,2.5) rot=(0,0,1;0rad)
  Sketch = -> Sketch028
  Type = 0
FEATURE [Sketcher::SketchObject] Sketch029
  Placement = pos=(85,0,0) rot=(0.57735,0.57735,0.57735;2.0944rad)
  sketch-geometry (8):
    g0: LineSegment StartX=2.5 StartY=57.5 StartZ=0 EndX=32.5 EndY=57.5 EndZ=0
    g1: LineSegment StartX=32.5 StartY=57.5 StartZ=0 EndX=32.5 EndY=2.5 EndZ=0
    g2: LineSegment StartX=32.5 StartY=2.5 StartZ=0 EndX=2.5 EndY=2.5 EndZ=0
    g3: LineSegment StartX=2.5 StartY=2.5 StartZ=0 EndX=2.5 EndY=57.5 EndZ=0
    g4: LineSegment StartX=10 StartY=50 StartZ=0 EndX=25 EndY=50 EndZ=0
    g5: LineSegment StartX=25 StartY=50 StartZ=0 EndX=25 EndY=10 EndZ=0
    g6: LineSegment StartX=25 StartY=10 StartZ=0 EndX=10 EndY=10 EndZ=0
    g7: LineSegment StartX=10 StartY=10 StartZ=0 EndX=10 EndY=50 EndZ=0
  constraints (24):
    c: Coincident(g0,g1)
    c: Coincident(g1,g2)
    c: Coincident(g2,g3)
    c: Coincident(g3,g0)
    c: Horizontal(g0)
    c: Horizontal(g2)
    c: Vertical(g1)
    c: Vertical(g3)
    c: DistanceX(g0,g0) = 30
    c: DistanceY(g1,g1) = 55
    c: DistanceX(g-1,g2) = 2.5
    c: DistanceY(g-1,g2) = 2.5
    c: Coincident(g4,g5)
    c: Coincident(g5,g6)
    c: Coincident(g6,g7)
    c: Coincident(g7,g4)
    c: Horizontal(g4)
    c: Horizontal(g6)
    c: Vertical(g5)
    c: Vertical(g7)
    c: DistanceX(g4) = 15
    c: DistanceY(g7) = 40
    c: DistanceX(g5,g1) = 7.5
    c: DistanceY(g5,g1) = -7.5
FEATURE [PartDesign::Pad] Pad029
  Length = 2.5
  Length2 = 100
  Placement = pos=(85,0,0) rot=(0.57735,0.57735,0.57735;2.0944rad)
  Sketch = -> Sketch029
  Type = 0
FEATURE [Sketcher::SketchObject] Sketch030
  Placement = pos=(0,35,0) rot=(1,0,0;1.5708rad)
  sketch-geometry (8):
    g0: LineSegment StartX=22.5 StartY=57.5 StartZ=0 EndX=87.5 EndY=57.5 EndZ=0
    g1: LineSegment StartX=87.5 StartY=57.5 StartZ=0 EndX=87.5 EndY=2.5 EndZ=0
    g2: LineSegment StartX=87.5 StartY=2.5 StartZ=0 EndX=22.5 EndY=2.5 EndZ=0
    g3: LineSegment StartX=22.5 StartY=2.5 StartZ=0 EndX=22.5 EndY=57.5 EndZ=0
    g4: LineSegment StartX=32.5 StartY=47.5 StartZ=0 EndX=47.5 EndY=47.5 EndZ=0
    g5: LineSegment StartX=47.5 StartY=47.5 StartZ=0 EndX=47.5 EndY=12.5 EndZ=0
    g6: LineSegment StartX=47.5 StartY=12.5 StartZ=0 EndX=32.5 EndY=12.5 EndZ=0
    g7: LineSegment StartX=32.5 StartY=12.5 StartZ=0 EndX=32.5 EndY=47.5 EndZ=0
  constraints (24):
    c: Coincident(g0,g1)
    c: Coincident(g1,g2)
    c: Coincident(g2,g3)
    c: Coincident(g3,g0)
    c: Horizontal(g0)
    c: Horizontal(g2)
    c: Vertical(g1)
    c: Vertical(g3)
    c: DistanceX(g-1,g0) = 22.5
    c: DistanceX(g0,g0) = 65
    c: DistanceY(g1,g1) = 55
    c: DistanceY(g-1,g1) = 2.5
    c: Coincident(g4,g5)
    c: Coincident(g5,g6)
    c: Coincident(g6,g7)
    c: Coincident(g7,g4)
    c: Horizontal(g4)
    c: Horizontal(g6)
    c: Vertical(g5)
    c: Vertical(g7)
    c: DistanceX(g4) = 15
    c: DistanceY(g7) = 35
    c: DistanceX(g5,g1) = 40
    c: DistanceY(g1,g5) = 10
FEATURE [PartDesign::Pad] Pad030
  Length = 2.5
  Length2 = 100
  Placement = pos=(0,35,0) rot=(1,0,0;1.5708rad)
  Sketch = -> Sketch030
  Type = 0
FEATURE [Sketcher::SketchObject] Sketch031
  Placement = pos=(22.5,0,0) rot=(0.57735,0.57735,0.57735;2.0944rad)
  sketch-geometry (8):
    g0: LineSegment StartX=2.5 StartY=57.5 StartZ=0 EndX=32.5 EndY=57.5 EndZ=0
    g1: LineSegment StartX=32.5 StartY=57.5 StartZ=0 EndX=32.5 EndY=2.5 EndZ=0
    g2: LineSegment StartX=32.5 StartY=2.5 StartZ=0 EndX=2.5 EndY=2.5 EndZ=0
    g3: LineSegment StartX=2.5 StartY=57.5 StartZ=0 EndX=2.5 EndY=47.5 EndZ=0
    g4: LineSegment StartX=2.5 StartY=47.5 StartZ=0 EndX=5 EndY=47.5 EndZ=0
    g5: LineSegment StartX=5 StartY=47.5 StartZ=0 EndX=5 EndY=37.5 EndZ=0
    g6: LineSegment StartX=5 StartY=37.5 StartZ=0 EndX=2.5 EndY=37.5 EndZ=0
    g7: LineSegment StartX=2.5 StartY=37.5 StartZ=0 EndX=2.5 EndY=2.5 EndZ=0
  constraints (24):
    c: Coincident(g0,g1)
    c: Coincident(g1,g2)
    c: Horizontal(g0)
    c: Horizontal(g2)
    c: Vertical(g1)
    c: DistanceX(g0,g0) = 30
    c: DistanceY(g1,g1) = 55
    c: DistanceX(g-1,g2) = 2.5
    c: DistanceY(g-1,g2) = 2.5
    c: Vertical(g3)
    c: Coincident(g3,g4)
    c: Horizontal(g4)
    c: Coincident(g4,g5)
    c: Vertical(g5)
    c: Coincident(g5,g6)
    c: Horizontal(g6)
    c: Coincident(g6,g7)
    c: Vertical(g7)
    c: Coincident(g2,g7)
    c: Coincident(g0,g3)
    c: Equal(g6,g4)
    c: DistanceY(g3,g3) = 10
    c: DistanceY(g5,g5) = 10
    c: DistanceX(g4,g4) = 2.5
FEATURE [PartDesign::Pad] Pad031
  Length = 2.5
  Length2 = 100
  Placement = pos=(22.5,0,0) rot=(0.57735,0.57735,0.57735;2.0944rad)
  Sketch = -> Sketch031
  Type = 0
FEATURE [Sketcher::SketchObject] Sketch032
  Placement = pos=(0,0,55) rot=(0,0,1;0rad)
  sketch-geometry (4):
    g0: LineSegment StartX=25 StartY=32.5 StartZ=0 EndX=85 EndY=32.5 EndZ=0
    g1: LineSegment StartX=85 StartY=32.5 StartZ=0 EndX=85 EndY=2.5 EndZ=0
    g2: LineSegment StartX=85 StartY=2.5 StartZ=0 EndX=25 EndY=2.5 EndZ=0
    g3: LineSegment StartX=25 StartY=2.5 StartZ=0 EndX=25 EndY=32.5 EndZ=0
  constraints (12):
    c: Coincident(g0,g1)
    c: Coincident(g1,g2)
    c: Coincident(g2,g3)
    c: Coincident(g3,g0)
    c: Horizontal(g0)
    c: Horizontal(g2)
    c: Vertical(g1)
    c: Vertical(g3)
    c: DistanceY(g-1,g1) = 2.5
    c: DistanceX(g0,g0) = 60
    c: DistanceY(g3,g3) = 30
    c: DistanceX(g-1,g0) = 25
FEATURE [PartDesign::Pad] Pad032
  Length = 2.5
  Length2 = 100
  Placement = pos=(0,0,55) rot=(0,0,1;0rad)
  Sketch = -> Sketch032
  Type = 0
FEATURE [App::DocumentObjectGroup] Group008  label="CtrlBox"
  Group = -> [Pad027,Pad028,Pad029,Pad031,Pad032]
FEATURE [Sketcher::SketchObject] Sketch033
  Placement = pos=(-25,0,0) rot=(0.57735,0.57735,0.57735;2.0944rad)
  sketch-geometry (2):
    g0: Circle CenterX=55 CenterY=-30 CenterZ=0 NormalX=0 NormalY=0 NormalZ=1 Radius=20
    g1: Circle CenterX=55 CenterY=-30 CenterZ=0 NormalX=0 NormalY=0 NormalZ=1 Radius=2.5
  constraints (5):
    c: DistanceX(g0) = 55
    c: DistanceY(g0) = -30
    c: Radius(g0) = 20
    c: Coincident(g1,g0)
    c: Radius(g1) = 2.5
FEATURE [PartDesign::Pad] Pad033
  Length = 1
  Length2 = 100
  Placement = pos=(-25,0,0) rot=(0.57735,0.57735,0.57735;2.0944rad)
  Sketch = -> Sketch033
  Type = 0
FEATURE [Sketcher::SketchObject] Sketch034
  Placement = pos=(0,30,0) rot=(1,0,0;1.5708rad)
  sketch-geometry (5):
    g0: LineSegment StartX=-25 StartY=-10 StartZ=0 EndX=25 EndY=-10 EndZ=0
    g1: LineSegment StartX=25 StartY=-10 StartZ=0 EndX=25 EndY=-50 EndZ=0
    g2: LineSegment StartX=25 StartY=-50 StartZ=0 EndX=-25 EndY=-50 EndZ=0
    g3: LineSegment StartX=-25 StartY=-50 StartZ=0 EndX=-25 EndY=-10 EndZ=0
    g4: Circle CenterX=0 CenterY=-20 CenterZ=0 NormalX=0 NormalY=0 NormalZ=1 Radius=1.5
  constraints (15):
    c: Coincident(g0,g1)
    c: Coincident(g1,g2)
    c: Coincident(g2,g3)
    c: Coincident(g3,g0)
    c: Horizontal(g0)
    c: Horizontal(g2)
    c: Vertical(g1)
    c: Vertical(g3)
    c: Symmetric(g0,g0,g-2)
    c: DistanceX(g0) = 50
    c: DistanceY(g3) = 40
    c: DistanceY(g-1,g0) = -10
    c: PointOnObject(g4,g-2)
    c: Radius(g4) = 1.5
    c: DistanceY(g4) = -20
FEATURE [PartDesign::Pad] Pad034
  Length = 5
  Length2 = 100
  Placement = pos=(0,30,0) rot=(1,0,0;1.5708rad)
  Sketch = -> Sketch034
  Type = 0
FEATURE [App::DocumentObjectGroup] Group005  label="Socket"
  Group = -> [Pad008,Pad010,Clone010,Clone013,Pad033,Pad034]
FEATURE [Mesh::Feature] fa_130ra  label="fa-130ra"
  Placement = pos=(60,46.1604,29.9395) rot=(-1,0,0;1.5708rad)
FEATURE [Sketcher::SketchObject] Sketch035
  Placement = pos=(0,80,0) rot=(1,0,0;1.5708rad)
  sketch-geometry (1):
    g0: Circle CenterX=60 CenterY=30 CenterZ=0 NormalX=0 NormalY=0 NormalZ=1 Radius=20
  constraints (3):
    c: Radius(g0) = 20
    c: DistanceX(g0) = 60
    c: DistanceY(g0) = 30
FEATURE [PartDesign::Pad] Pad035
  Length = 10
  Length2 = 100
  Placement = pos=(0,80,0) rot=(1,0,0;1.5708rad)
  Sketch = -> Sketch035
  Type = 0
FEATURE [Sketcher::SketchObject] Sketch036
  Placement = pos=(85,0,0) rot=(0.57735,0.57735,0.57735;2.0944rad)
  sketch-geometry (4):
    g0: LineSegment StartX=35 StartY=57.5 StartZ=0 EndX=85 EndY=57.5 EndZ=0
    g1: LineSegment StartX=85 StartY=57.5 StartZ=0 EndX=85 EndY=2.5 EndZ=0
    g2: LineSegment StartX=85 StartY=2.5 StartZ=0 EndX=35 EndY=2.5 EndZ=0
    g3: LineSegment StartX=35 StartY=2.5 StartZ=0 EndX=35 EndY=57.5 EndZ=0
  constraints (12):
    c: Coincident(g0,g1)
    c: Coincident(g1,g2)
    c: Coincident(g2,g3)
    c: Coincident(g3,g0)
    c: Horizontal(g0)
    c: Horizontal(g2)
    c: Vertical(g1)
    c: Vertical(g3)
    c: DistanceX(g2) = 35
    c: DistanceY(g2) = 2.5
    c: DistanceX(g0) = 50
    c: DistanceY(g1) = -55
FEATURE [PartDesign::Pad] Pad036
  Length = 2.5
  Length2 = 100
  Placement = pos=(85,0,0) rot=(0.57735,0.57735,0.57735;2.0944rad)
  Sketch = -> Sketch036
  Type = 0
FEATURE [Part::FeaturePython] Clone026  label="Clone of Pad036"  # Draft clone (typed FeaturePython)
  Objects = -> [Pad036]
  Placement = pos=(30,0,0) rot=(0.57735,0.57735,0.57735;2.0944rad)
  Scale = (1,1,1)
FEATURE [Sketcher::SketchObject] Sketch037
  Placement = pos=(0,0,2.5) rot=(0,0,1;0rad)
  sketch-geometry (8):
    g0: LineSegment StartX=32.5 StartY=85 StartZ=0 EndX=85 EndY=85 EndZ=0
    g1: LineSegment StartX=85 StartY=85 StartZ=0 EndX=85 EndY=35 EndZ=0
    g2: LineSegment StartX=32.5 StartY=35 StartZ=0 EndX=32.5 EndY=85 EndZ=0
    g3: LineSegment StartX=32.5 StartY=35 StartZ=0 EndX=42.5 EndY=35 EndZ=0
    g4: LineSegment StartX=42.5 StartY=35 StartZ=0 EndX=42.5 EndY=37.54 EndZ=0
    g5: LineSegment StartX=42.5 StartY=37.54 StartZ=0 EndX=50.12 EndY=37.54 EndZ=0
    g6: LineSegment StartX=50.12 StartY=37.54 StartZ=0 EndX=50.12 EndY=35 EndZ=0
    g7: LineSegment StartX=50.12 StartY=35 StartZ=0 EndX=85 EndY=35 EndZ=0
  constraints (24):
    c: Coincident(g0,g1)
    c: Coincident(g2,g0)
    c: Horizontal(g0)
    c: Vertical(g1)
    c: Vertical(g2)
    c: DistanceX(g2) = 32.5
    c: DistanceY(g2) = 35
    c: DistanceX(g0) = 52.5
    c: DistanceY(g1) = -50
    c: Horizontal(g3)
    c: Coincident(g3,g4)
    c: Vertical(g4)
    c: Coincident(g4,g5)
    c: Horizontal(g5)
    c: Coincident(g5,g6)
    c: Vertical(g6)
    c: Coincident(g6,g7)
    c: Horizontal(g7)
    c: Coincident(g1,g7)
    c: Coincident(g2,g3)
    c: DistanceY(g6) = -2.54
    c: DistanceY(g4) = 2.54
    c: DistanceX(g5) = 7.62
    c: DistanceX(g3) = 10
FEATURE [PartDesign::Pad] Pad037
  Length = 2.5
  Length2 = 100
  Placement = pos=(0,0,2.5) rot=(0,0,1;0rad)
  Sketch = -> Sketch037
  Type = 0
FEATURE [Sketcher::SketchObject] Sketch038
  Placement = pos=(0,90,0) rot=(1,0,0;1.5708rad)
  sketch-geometry (8):
    g0: LineSegment StartX=30 StartY=57.5 StartZ=0 EndX=87.5 EndY=57.5 EndZ=0
    g1: LineSegment StartX=87.5 StartY=57.5 StartZ=0 EndX=87.5 EndY=2.5 EndZ=0
    g2: LineSegment StartX=87.5 StartY=2.5 StartZ=0 EndX=30 EndY=2.5 EndZ=0
    g3: LineSegment StartX=30 StartY=2.5 StartZ=0 EndX=30 EndY=57.5 EndZ=0
    g4: LineSegment StartX=40 StartY=50 StartZ=0 EndX=80 EndY=50 EndZ=0
    g5: LineSegment StartX=80 StartY=50 StartZ=0 EndX=80 EndY=10 EndZ=0
    g6: LineSegment StartX=80 StartY=10 StartZ=0 EndX=40 EndY=10 EndZ=0
    g7: LineSegment StartX=40 StartY=10 StartZ=0 EndX=40 EndY=50 EndZ=0
  constraints (24):
    c: Coincident(g0,g1)
    c: Coincident(g1,g2)
    c: Coincident(g2,g3)
    c: Coincident(g3,g0)
    c: Horizontal(g0)
    c: Horizontal(g2)
    c: Vertical(g1)
    c: Vertical(g3)
    c: DistanceX(g2) = 30
    c: DistanceY(g2) = 2.5
    c: DistanceY(g1) = -55
    c: DistanceX(g0) = 57.5
    c: Coincident(g4,g5)
    c: Coincident(g5,g6)
    c: Coincident(g6,g7)
    c: Coincident(g7,g4)
    c: Horizontal(g4)
    c: Horizontal(g6)
    c: Vertical(g5)
    c: Vertical(g7)
    c: DistanceX(g4) = 40
    c: DistanceY(g7) = 40
    c: DistanceY(g4,g0) = 7.5
    c: DistanceX(g4,g0) = 7.5
FEATURE [PartDesign::Pad] Pad038
  Length = 5
  Length2 = 100
  Placement = pos=(0,90,0) rot=(1,0,0;1.5708rad)
  Sketch = -> Sketch038
  Type = 0
FEATURE [Sketcher::SketchObject] Sketch039
  Placement = pos=(0,0,37.5) rot=(0,0,1;0rad)
  sketch-geometry (4):
    g0: LineSegment StartX=47.5 StartY=60 StartZ=0 EndX=85 EndY=60 EndZ=0
    g1: LineSegment StartX=85 StartY=60 StartZ=0 EndX=85 EndY=35 EndZ=0
    g2: LineSegment StartX=85 StartY=35 StartZ=0 EndX=47.5 EndY=35 EndZ=0
    g3: LineSegment StartX=47.5 StartY=35 StartZ=0 EndX=47.5 EndY=60 EndZ=0
  constraints (12):
    c: Coincident(g0,g1)
    c: Coincident(g1,g2)
    c: Coincident(g2,g3)
    c: Coincident(g3,g0)
    c: Horizontal(g0)
    c: Horizontal(g2)
    c: Vertical(g1)
    c: Vertical(g3)
    c: DistanceX(g2) = 47.5
    c: DistanceY(g2) = 35
    c: DistanceX(g0) = 37.5
    c: DistanceY(g1) = -25
FEATURE [PartDesign::Pad] Pad039
  Length = 2.5
  Length2 = 100
  Placement = pos=(0,0,37.5) rot=(0,0,1;0rad)
  Sketch = -> Sketch039
  Type = 0
FEATURE [Sketcher::SketchObject] Sketch040
  Placement = pos=(0,0,20) rot=(0,0,1;0rad)
  sketch-geometry (8):
    g0: LineSegment StartX=47.5 StartY=60 StartZ=0 EndX=85 EndY=60 EndZ=0
    g1: LineSegment StartX=85 StartY=60 StartZ=0 EndX=85 EndY=35 EndZ=0
    g2: LineSegment StartX=85 StartY=35 StartZ=0 EndX=47.5 EndY=35 EndZ=0
    g3: LineSegment StartX=47.5 StartY=35 StartZ=0 EndX=47.5 EndY=60 EndZ=0
    g4: LineSegment StartX=50.5 StartY=48 StartZ=0 EndX=70.5 EndY=48 EndZ=0
    g5: LineSegment StartX=70.5 StartY=48 StartZ=0 EndX=70.5 EndY=40 EndZ=0
    g6: LineSegment StartX=70.5 StartY=40 StartZ=0 EndX=50.5 EndY=40 EndZ=0
    g7: LineSegment StartX=50.5 StartY=40 StartZ=0 EndX=50.5 EndY=48 EndZ=0
  constraints (24):
    c: Coincident(g0,g1)
    c: Coincident(g1,g2)
    c: Coincident(g2,g3)
    c: Coincident(g3,g0)
    c: Horizontal(g0)
    c: Horizontal(g2)
    c: Vertical(g1)
    c: Vertical(g3)
    c: DistanceX(g2) = 47.5
    c: DistanceY(g2) = 35
    c: DistanceX(g0) = 37.5
    c: DistanceY(g1) = -25
    c: Coincident(g4,g5)
    c: Coincident(g5,g6)
    c: Coincident(g6,g7)
    c: Coincident(g7,g4)
    c: Horizontal(g4)
    c: Horizontal(g6)
    c: Vertical(g5)
    c: Vertical(g7)
    c: DistanceX(g2,g6) = 3
    c: DistanceY(g2,g6) = 5
    c: DistanceX(g4) = 20
    c: DistanceY(g5) = -8
FEATURE [PartDesign::Pad] Pad040
  Length = 2.5
  Length2 = 100
  Placement = pos=(0,0,20) rot=(0,0,1;0rad)
  Sketch = -> Sketch040
  Type = 0
FEATURE [Sketcher::SketchObject] Sketch041
  Placement = pos=(0,0,5) rot=(0,0,1;0rad)
  sketch-geometry (4):
    g0: LineSegment StartX=35 StartY=32.5 StartZ=0 EndX=75 EndY=32.5 EndZ=0
    g1: LineSegment StartX=75 StartY=32.5 StartZ=0 EndX=75 EndY=28.5 EndZ=0
    g2: LineSegment StartX=75 StartY=28.5 StartZ=0 EndX=35 EndY=28.5 EndZ=0
    g3: LineSegment StartX=35 StartY=28.5 StartZ=0 EndX=35 EndY=32.5 EndZ=0
  constraints (12):
    c: Coincident(g0,g1)
    c: Coincident(g1,g2)
    c: Coincident(g2,g3)
    c: Coincident(g3,g0)
    c: Horizontal(g0)
    c: Horizontal(g2)
    c: Vertical(g1)
    c: Vertical(g3)
    c: DistanceX(g0) = 35
    c: DistanceY(g0) = 32.5
    c: DistanceX(g2) = -40
    c: DistanceY(g1) = -4
FEATURE [PartDesign::Pad] Pad041
  Length = 5
  Length2 = 100
  Placement = pos=(0,0,5) rot=(0,0,1;0rad)
  Sketch = -> Sketch041
  Type = 0
FEATURE [Part::FeaturePython] Clone028  label="Clone of Pad041"  # Draft clone (typed FeaturePython)
  Objects = -> [Pad041]
  Placement = pos=(0,0,50) rot=(0,0,1;0rad)
  Scale = (1,1,1)
FEATURE [Sketcher::SketchObject] Sketch042
  Placement = pos=(0,32.5,0) rot=(1,0,0;1.5708rad)
  sketch-geometry (4):
    g0: LineSegment StartX=81 StartY=47.5 StartZ=0 EndX=85 EndY=47.5 EndZ=0
    g1: LineSegment StartX=85 StartY=47.5 StartZ=0 EndX=85 EndY=12.5 EndZ=0
    g2: LineSegment StartX=85 StartY=12.5 StartZ=0 EndX=81 EndY=12.5 EndZ=0
    g3: LineSegment StartX=81 StartY=12.5 StartZ=0 EndX=81 EndY=47.5 EndZ=0
  constraints (12):
    c: Coincident(g0,g1)
    c: Coincident(g1,g2)
    c: Coincident(g2,g3)
    c: Coincident(g3,g0)
    c: Horizontal(g0)
    c: Horizontal(g2)
    c: Vertical(g1)
    c: Vertical(g3)
    c: DistanceX(g0) = 4
    c: DistanceX(g2) = 81
    c: DistanceY(g2) = 12.5
    c: DistanceY(g1) = -35
FEATURE [PartDesign::Pad] Pad042
  Length = 4
  Length2 = 100
  Placement = pos=(0,32.5,0) rot=(1,0,0;1.5708rad)
  Sketch = -> Sketch042
  Type = 0
FEATURE [Sketcher::SketchObject] Sketch043
  Placement = pos=(0,0,55) rot=(0,0,1;0rad)
  sketch-geometry (4):
    g0: LineSegment StartX=32.5 StartY=85 StartZ=0 EndX=85 EndY=85 EndZ=0
    g1: LineSegment StartX=85 StartY=85 StartZ=0 EndX=85 EndY=35 EndZ=0
    g2: LineSegment StartX=85 StartY=35 StartZ=0 EndX=32.5 EndY=35 EndZ=0
    g3: LineSegment StartX=32.5 StartY=35 StartZ=0 EndX=32.5 EndY=85 EndZ=0
  constraints (12):
    c: Coincident(g0,g1)
    c: Coincident(g1,g2)
    c: Coincident(g2,g3)
    c: Coincident(g3,g0)
    c: Horizontal(g0)
    c: Horizontal(g2)
    c: Vertical(g1)
    c: Vertical(g3)
    c: DistanceX(g2) = 32.5
    c: DistanceY(g2) = 35
    c: DistanceX(g0) = 52.5
    c: DistanceY(g1) = -50
FEATURE [PartDesign::Pad] Pad043
  Length = 2.5
  Length2 = 100
  Placement = pos=(0,0,55) rot=(0,0,1;0rad)
  Sketch = -> Sketch043
  Type = 0
FEATURE [App::DocumentObjectGroup] Group009  label="FanBox"
  Group = -> [Pad030,fa_130ra,Pad035,Pad036,Clone026,Pad037,Pad038,Pad039,Pad040,Pad041,Clone028,Pad042,Pad043]
